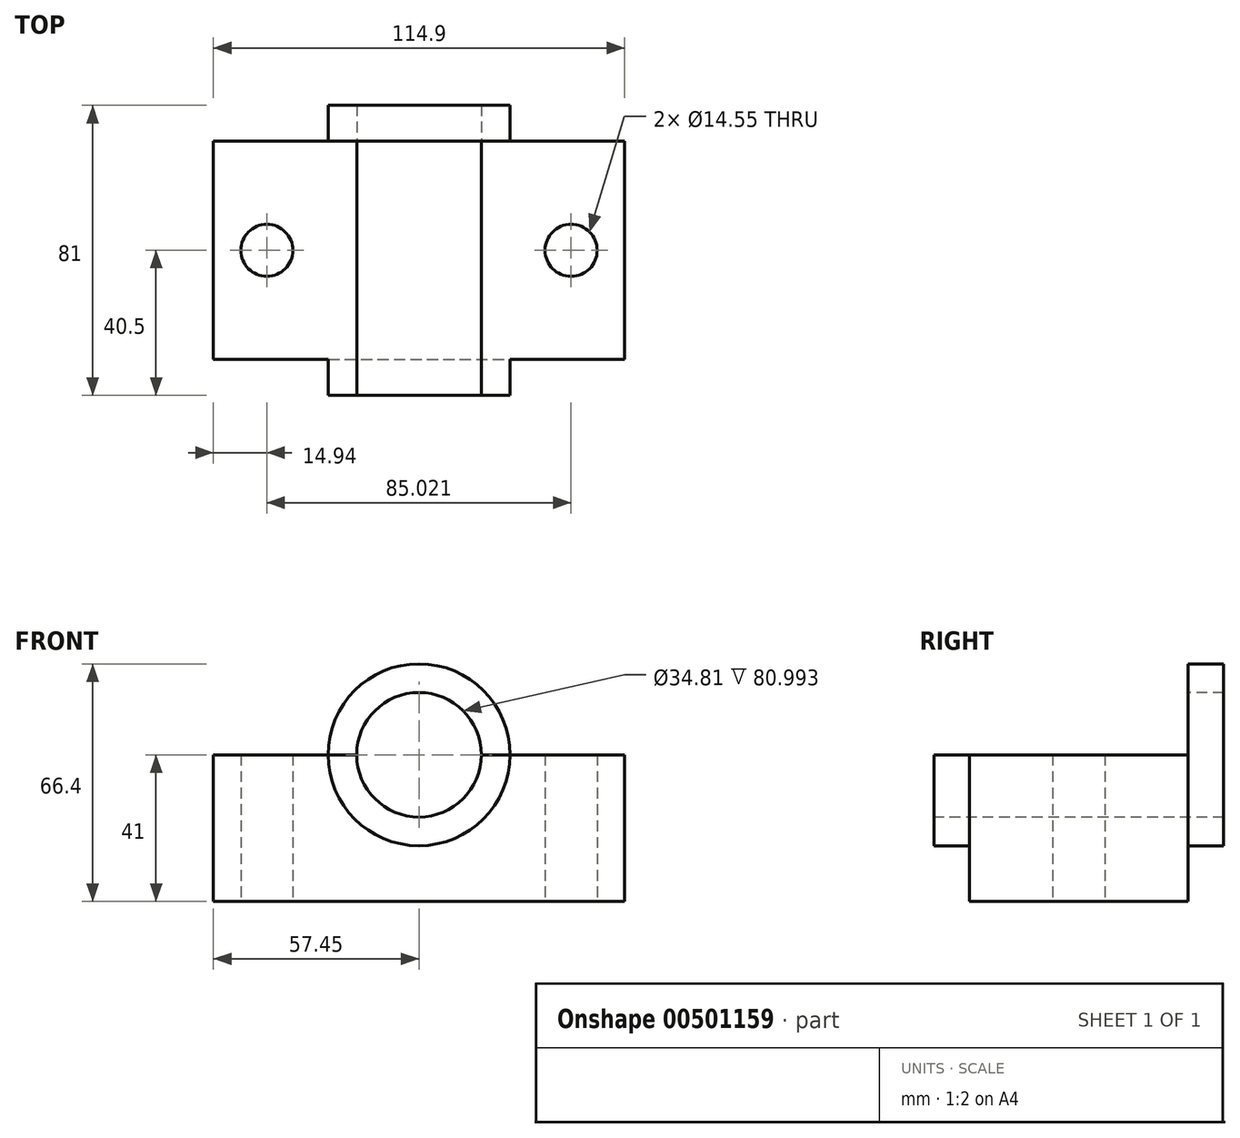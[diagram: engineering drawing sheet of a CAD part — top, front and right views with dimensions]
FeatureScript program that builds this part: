
annotation { "Feature Type Name" : "Feature", "Feature Type Description" : "" }
export const myFeature = defineFeature(function(context is Context, id is Id, definition is map)
    precondition{}
    {
        {
            var Q0;
            Q0=qCreatedBy(makeId("Top.planeOp"),FACE);
            var sketch = newSketch(context, id + "F0", { "sketchPlane" : qUnion([Q0])});
            skLineSegment(sketch, "E0.bottom", {"start": v(-57.45, 30.5) * mm, "end": v(57.45, 30.5) * mm});
            skLineSegment(sketch, "E0.top", {"start": v(-57.45, -30.5) * mm, "end": v(57.45, -30.5) * mm});
            skLineSegment(sketch, "E0.left", {"start": v(-57.45, 30.5) * mm, "end": v(-57.45, -30.5) * mm});
            skLineSegment(sketch, "E0.right", {"start": v(57.45, 30.5) * mm, "end": v(57.45, -30.5) * mm});
            skPoint(sketch, "E0.middle", {"position": v(0, 0) * mm});
            skCircle(sketch, "E1", {"center": v(-42.51, 0) * mm, "radius": 7.28 * mm});
            skCircle(sketch, "E2", {"center": v(42.51, 0) * mm, "radius": 7.28 * mm});
            skLineSegment(sketch, "E3", {"start": v(-42.51, 0) * mm, "end": v(42.51, 0) * mm, "construction": true});
            skSolve(sketch);
        }
        {
            var Q0;
            Q0=makeQuery(id+"F0.imprint","IMPRINT",FACE,{"disambiguationData":[TD([[makeQuery(id+"F0.imprint","IMPRINT",EDGE,{"derivedFrom":sQuery(id+"F0.wireOp",EDGE,"E0.bottom")}),-1.0]])]});
            extrude(context, id + "F1", {"entities" : qUnion([Q0]), "depth" : 41 * mm});
        }
        {
            var Q0;
            Q0=makeQuery(id+"F1.opExtrude","SWEPT_FACE",FACE,{"disambiguationData":[OSD([sQuery(id+"F0.wireOp",EDGE,"E0.top")])]});
            var sketch = newSketch(context, id + "F2", { "sketchPlane" : qUnion([Q0])});
            skCircle(sketch, "E4", {"center": v(0, 41) * mm, "radius": 17.4 * mm});
            skCircle(sketch, "E5.0", {"center": v(0, 41) * mm, "radius": 25.4 * mm});
            skSolve(sketch);
        }
        {
            var Q0;
            {var subQ0=sQuery(id+"F2.wireOp",EDGE,"E4");var subQ1=makeQuery(id+"F1.opExtrude","CAP_EDGE",EDGE,{"disambiguationData":[OSD([sQuery(id+"F0.wireOp",EDGE,"E0.top")])],"isStart":false});var subQ2=makeQuery(id+"F2.imprint","INTERSECT",VERTEX,{"disambiguationData":[OD(0.0)],"derivedFrom":[subQ1,subQ0]});Q0=makeQuery(id+"F2.imprint","IMPRINT",FACE,{"disambiguationData":[TD([[makeQuery(id+"F2.imprint","IMPRINT",EDGE,{"disambiguationData":[TD([[subQ2,-1.0]])],"derivedFrom":subQ0}),1.0]])]});}
            extrude(context, id + "F3", {"entities" : qUnion([Q0]), "operationType" : NewBodyOperationType.REMOVE, "endBound" : BoundingType.THROUGH_ALL, "oppositeDirection" : true, "depth" : 25 * mm});
        }
        {
            var Q0;
            {var subQ0=sQuery(id+"F2.wireOp",EDGE,"E4");var subQ1=makeQuery(id+"F1.opExtrude","CAP_EDGE",EDGE,{"disambiguationData":[OSD([sQuery(id+"F0.wireOp",EDGE,"E0.top")])],"isStart":false});var subQ2=makeQuery(id+"F2.imprint","INTERSECT",VERTEX,{"disambiguationData":[OD(0.0)],"derivedFrom":[subQ1,subQ0]});Q0=makeQuery(id+"F2.imprint","IMPRINT",FACE,{"disambiguationData":[TD([[makeQuery(id+"F2.imprint","IMPRINT",EDGE,{"disambiguationData":[TD([[subQ2,-1.0]])],"derivedFrom":subQ0}),-1.0]])]});}
            extrude(context, id + "F4", {"entities" : qUnion([Q0]), "operationType" : NewBodyOperationType.ADD, "depth" : 10 * mm});
        }
        {
            var Q0;
            Q0=makeQuery(id+"F1.opExtrude","SWEPT_FACE",FACE,{"disambiguationData":[OSD([sQuery(id+"F0.wireOp",EDGE,"E0.bottom")])]});
            var sketch = newSketch(context, id + "F5", { "sketchPlane" : qUnion([Q0])});
            skCircle(sketch, "E6.0", {"center": v(0, 41) * mm, "radius": 25.4 * mm});
            skCircle(sketch, "E7.0", {"center": v(0, 41) * mm, "radius": 17.4 * mm});
            skSolve(sketch);
        }
        {
            var Q0;
            {var subQ12=sQuery(id+"F5.wireOp",EDGE,"E7.0");Q0=makeQuery(id+"F5.imprint","IMPRINT",FACE,{"disambiguationData":[TD([[makeQuery(id+"F5.imprint","IMPRINT",EDGE,{"disambiguationData":[OD(0.0)],"derivedFrom":subQ12}),-1.0]])]});}
            extrude(context, id + "F6", {"entities" : qUnion([Q0]), "operationType" : NewBodyOperationType.ADD, "depth" : 10 * mm});
        }
    });
